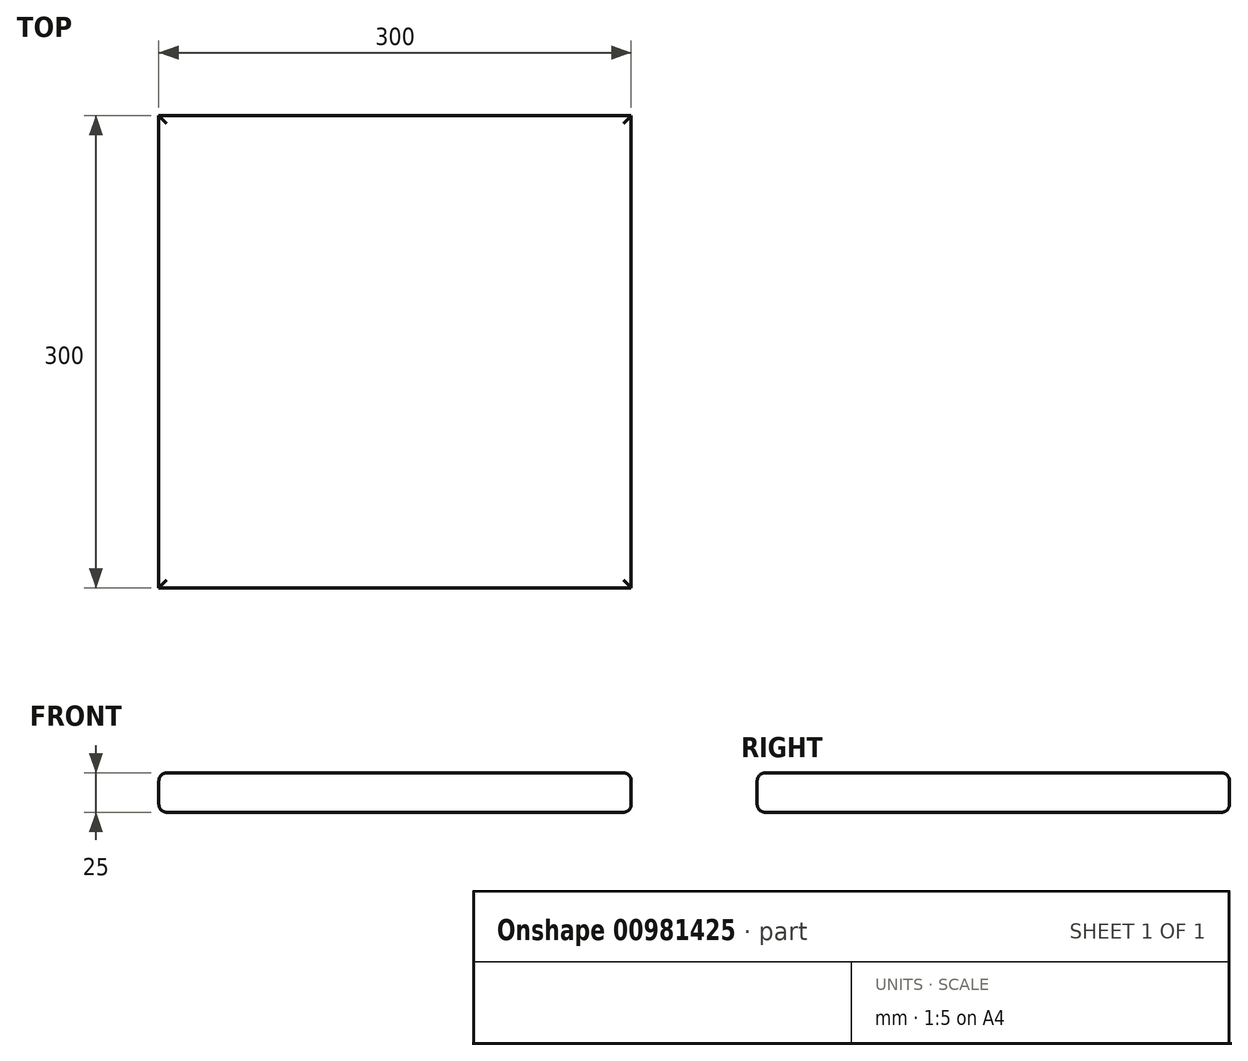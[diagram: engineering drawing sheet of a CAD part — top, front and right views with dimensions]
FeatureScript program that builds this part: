
annotation { "Feature Type Name" : "Feature", "Feature Type Description" : "" }
export const myFeature = defineFeature(function(context is Context, id is Id, definition is map)
    precondition{}
    {
        {
            var Q0;
            Q0=qCreatedBy(makeId("Top.planeOp"),FACE);
            var sketch = newSketch(context, id + "F0", { "sketchPlane" : qUnion([Q0])});
            skLineSegment(sketch, "E0.bottom", {"start": v(-150, 150) * mm, "end": v(150, 150) * mm});
            skLineSegment(sketch, "E0.top", {"start": v(-150, -150) * mm, "end": v(150, -150) * mm});
            skLineSegment(sketch, "E0.left", {"start": v(-150, 150) * mm, "end": v(-150, -150) * mm});
            skLineSegment(sketch, "E0.right", {"start": v(150, 150) * mm, "end": v(150, -150) * mm});
            skPoint(sketch, "E0.middle", {"position": v(0, 0) * mm});
            skSolve(sketch);
        }
        {
            var Q0;
            Q0 = qSketchRegion(id + "F0", true);
            extrude(context, id + "F1", {"entities" : qUnion([Q0]), "depth" : 25 * mm, "offsetDistance" : 25 * mm});
        }
        {
            var Q0;
            Q0=makeQuery(id+"F1.opExtrude","CAP_FACE",FACE,{"disambiguationData":[OSD([sQuery(id+"F0.wireOp",EDGE,"E0.bottom"),sQuery(id+"F0.wireOp",EDGE,"E0.top"),sQuery(id+"F0.wireOp",EDGE,"E0.left"),sQuery(id+"F0.wireOp",EDGE,"E0.right")])],"isStart":false});
            var Q1;
            Q1=makeQuery(id+"F1.opExtrude","CAP_FACE",FACE,{"disambiguationData":[OSD([sQuery(id+"F0.wireOp",EDGE,"E0.bottom"),sQuery(id+"F0.wireOp",EDGE,"E0.top"),sQuery(id+"F0.wireOp",EDGE,"E0.left"),sQuery(id+"F0.wireOp",EDGE,"E0.right")])],"isStart":true});
            fillet(context, id + "F2", {"entities" : qUnion([Q0, Q1]), "radius" : 5 * mm, "tangentPropagation" : true, "allowEdgeOverflow" : false});
        }
    });
